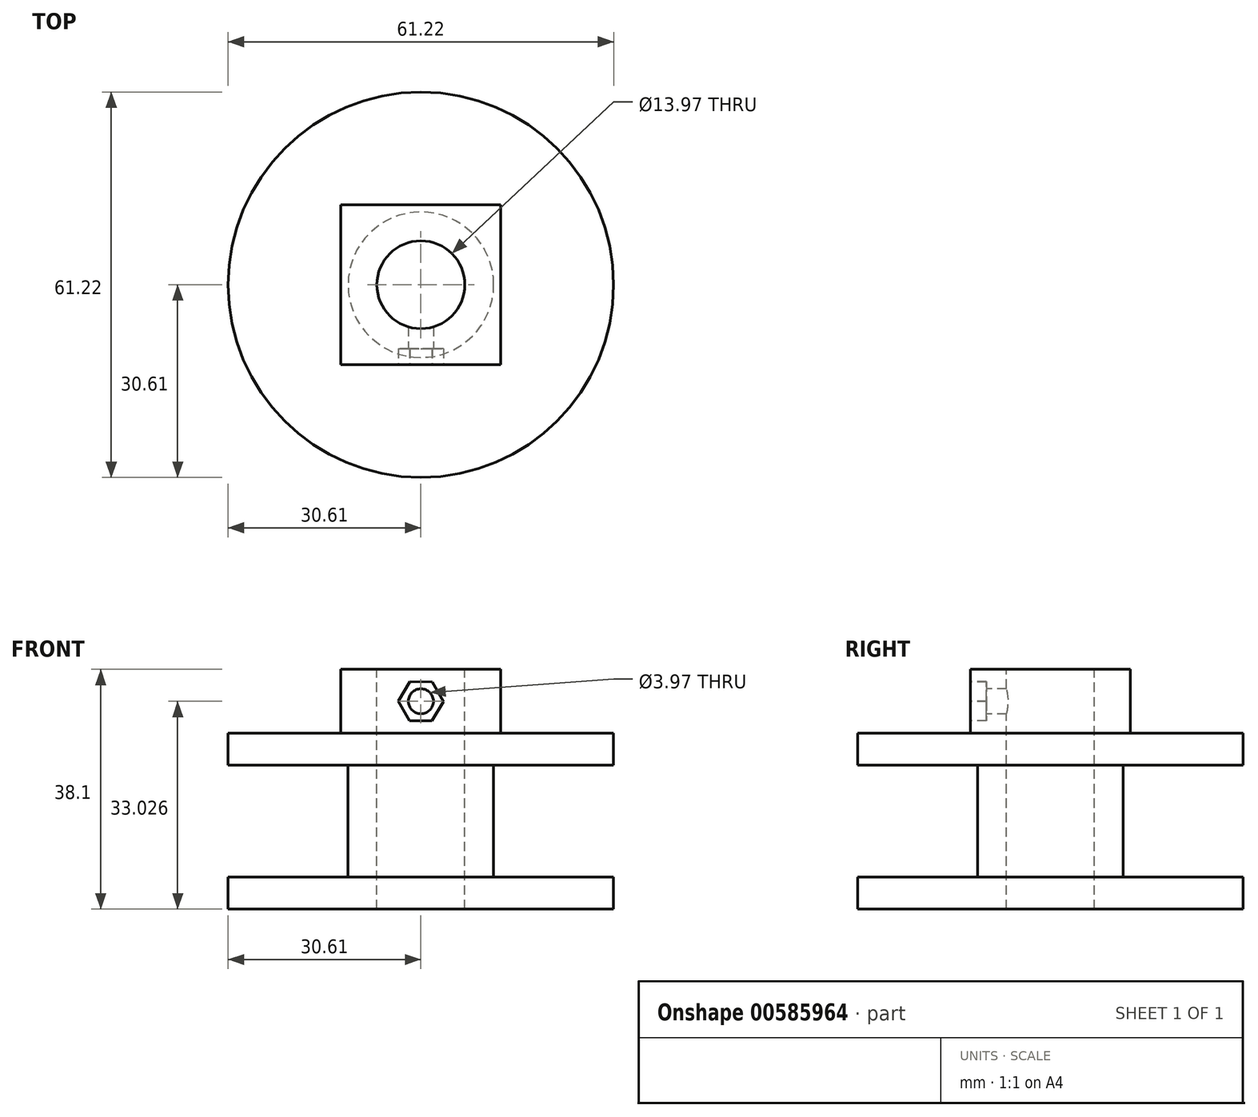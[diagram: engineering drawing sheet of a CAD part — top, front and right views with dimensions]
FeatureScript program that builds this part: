
annotation { "Feature Type Name" : "Feature", "Feature Type Description" : "" }
export const myFeature = defineFeature(function(context is Context, id is Id, definition is map)
    precondition{}
    {
        {
            var Q0;
            Q0=qCreatedBy(makeId("Front.planeOp"),FACE);
            var sketch = newSketch(context, id + "F0", { "sketchPlane" : qUnion([Q0])});
            skLineSegment(sketch, "E0.bottom", {"start": v(0, 0) * mm, "end": v(6.48, 0) * mm});
            skLineSegment(sketch, "E0.top", {"start": v(0, 38.1) * mm, "end": v(6.48, 38.1) * mm});
            skLineSegment(sketch, "E0.left", {"start": v(0, 0) * mm, "end": v(0, 38.1) * mm});
            skLineSegment(sketch, "E0.right", {"start": v(6.48, 0) * mm, "end": v(6.48, 38.1) * mm});
            skLineSegment(sketch, "E1.bottom", {"start": v(6.48, 38.1) * mm, "end": v(11.56, 38.1) * mm});
            skLineSegment(sketch, "E1.top", {"start": v(6.48, 0) * mm, "end": v(11.56, 0) * mm});
            skLineSegment(sketch, "E1.left", {"start": v(6.48, 38.1) * mm, "end": v(6.48, 0) * mm});
            skLineSegment(sketch, "E1.right", {"start": v(11.56, 38.1) * mm, "end": v(11.56, 0) * mm});
            skLineSegment(sketch, "E2.bottom", {"start": v(11.56, 0) * mm, "end": v(30.6, 0) * mm});
            skLineSegment(sketch, "E2.top", {"start": v(11.56, 5.08) * mm, "end": v(30.6, 5.08) * mm});
            skLineSegment(sketch, "E2.left", {"start": v(11.56, 0) * mm, "end": v(11.56, 5.08) * mm});
            skLineSegment(sketch, "E2.right", {"start": v(30.6, 0) * mm, "end": v(30.6, 5.08) * mm});
            skLineSegment(sketch, "E3", {"start": v(11.56, 5.08) * mm, "end": v(11.56, 22.86) * mm});
            skLineSegment(sketch, "E4.bottom", {"start": v(11.56, 22.86) * mm, "end": v(30.6, 22.86) * mm});
            skLineSegment(sketch, "E4.top", {"start": v(11.56, 27.94) * mm, "end": v(30.6, 27.94) * mm});
            skLineSegment(sketch, "E4.left", {"start": v(11.56, 22.86) * mm, "end": v(11.56, 27.94) * mm});
            skLineSegment(sketch, "E4.right", {"start": v(30.6, 22.86) * mm, "end": v(30.6, 27.94) * mm});
            skSolve(sketch);
        }
        {
            var Q0;
            Q0 = qSketchRegion(id + "F0", true);
            var Q1;
            Q1=sQuery(id+"F0.wireOp",EDGE,"E0.left");
            revolve(context, id + "F1", {"entities" : qUnion([Q0]), "axis" : qUnion([Q1]), "revolveType" : RevolveType.FULL});
        }
        {
            var Q0;
            Q0=makeQuery(id+"F1.opRevolve","SWEPT_FACE",FACE,{"disambiguationData":[OSD([sQuery(id+"F0.wireOp",EDGE,"E0.top"),sQuery(id+"F0.wireOp",EDGE,"E1.bottom")])]});
            var sketch = newSketch(context, id + "F2", { "sketchPlane" : qUnion([Q0])});
            skSolve(sketch);
        }
        {
            var Q0;
            Q0=makeQuery(id+"F2.imprint","IMPRINT",FACE,{"disambiguationData":[TD([[makeQuery(id+"F2.imprint","IMPRINT",EDGE,{"derivedFrom":makeQuery(id+"F1.opRevolve","SWEPT_EDGE",EDGE,{"disambiguationData":[OSD([sQuery(id+"F0.wireOp",EDGE,"E1.bottom"),sQuery(id+"F0.wireOp",EDGE,"E1.right")])]})}),-1.0]])]});
            var sketch = newSketch(context, id + "F3", { "sketchPlane" : qUnion([Q0])});
            skCircle(sketch, "E5", {"center": v(0, 0) * mm, "radius": 6.99 * mm});
            skSolve(sketch);
        }
        {
            var Q0;
            Q0=sQuery(id+"F3.wireOp",VERTEX,"E5.center");
            var Q1;
            Q1=makeQuery(id+"F1.opRevolve","SWEPT_BODY",BODY,{"disambiguationData":[OSD([sQuery(id+"F0.wireOp",EDGE,"E0.bottom"),sQuery(id+"F0.wireOp",EDGE,"E0.top"),sQuery(id+"F0.wireOp",EDGE,"E0.left"),sQuery(id+"F0.wireOp",EDGE,"E1.bottom"),sQuery(id+"F0.wireOp",EDGE,"E1.top"),sQuery(id+"F0.wireOp",EDGE,"E1.right"),sQuery(id+"F0.wireOp",EDGE,"E2.bottom"),sQuery(id+"F0.wireOp",EDGE,"E2.top"),sQuery(id+"F0.wireOp",EDGE,"E2.right"),sQuery(id+"F0.wireOp",EDGE,"E3"),sQuery(id+"F0.wireOp",EDGE,"E4.bottom"),sQuery(id+"F0.wireOp",EDGE,"E4.top"),sQuery(id+"F0.wireOp",EDGE,"E4.right")])]});
            hole(context, id + "F4", {"style" : HoleStyle.SIMPLE, "endStyle" : HoleEndStyle.THROUGH, "holeDiameter" : 13.97 * mm, "majorDiameter" : 6.35 * mm, "isTappedThrough" : true, "tappedDepth" : 12.7 * mm, "tapClearance" : 3, "locations" : qUnion([Q0]), "scope" : qUnion([Q1])});
        }
        {
            var Q0;
            Q0=makeQuery(id+"F1.opRevolve","SWEPT_FACE",FACE,{"disambiguationData":[OSD([sQuery(id+"F0.wireOp",EDGE,"E4.top")])]});
            var sketch = newSketch(context, id + "F5", { "sketchPlane" : qUnion([Q0])});
            skLineSegment(sketch, "E6.bottom", {"start": v(12.7, -12.7) * mm, "end": v(-12.7, -12.7) * mm});
            skLineSegment(sketch, "E6.top", {"start": v(12.7, 12.7) * mm, "end": v(-12.7, 12.7) * mm});
            skLineSegment(sketch, "E6.left", {"start": v(12.7, -12.7) * mm, "end": v(12.7, 12.7) * mm});
            skLineSegment(sketch, "E6.right", {"start": v(-12.7, -12.7) * mm, "end": v(-12.7, 12.7) * mm});
            skPoint(sketch, "E6.middle", {"position": v(0, 0) * mm});
            skSolve(sketch);
        }
        {
            var Q0;
            Q0=makeQuery(id+"F5.imprint","IMPRINT",FACE,{"disambiguationData":[TD([[makeQuery(id+"F5.imprint","IMPRINT",EDGE,{"derivedFrom":sQuery(id+"F5.wireOp",EDGE,"E6.bottom")}),-1.0]])]});
            extrude(context, id + "F6", {"entities" : qUnion([Q0]), "operationType" : NewBodyOperationType.ADD, "depth" : 10.16 * mm, "offsetDistance" : 25.4 * mm});
        }
        {
            var Q0;
            Q0=makeQuery(id+"F6.opExtrude","SWEPT_FACE",FACE,{"disambiguationData":[OSD([sQuery(id+"F5.wireOp",EDGE,"E6.bottom")])]});
            var sketch = newSketch(context, id + "F7", { "sketchPlane" : qUnion([Q0])});
            skCircle(sketch, "E7.cCircle", {"center": v(0, 33.02) * mm, "radius": 3.57 * mm, "construction": true});
            skLineSegment(sketch, "E7.0", {"start": v(1.76, 29.91) * mm, "end": v(-1.8, 29.94) * mm});
            skLineSegment(sketch, "E7.1", {"start": v(-1.8, 29.94) * mm, "end": v(-3.57, 33.05) * mm});
            skLineSegment(sketch, "E7.2", {"start": v(-3.57, 33.05) * mm, "end": v(-1.76, 36.13) * mm});
            skLineSegment(sketch, "E7.3", {"start": v(-1.76, 36.13) * mm, "end": v(1.8, 36.1) * mm});
            skLineSegment(sketch, "E7.4", {"start": v(1.8, 36.1) * mm, "end": v(3.57, 33) * mm});
            skLineSegment(sketch, "E7.5", {"start": v(3.57, 33) * mm, "end": v(1.76, 29.91) * mm});
            skSolve(sketch);
        }
        {
            var Q0;
            Q0=makeQuery(id+"F7.imprint","IMPRINT",FACE,{"disambiguationData":[TD([[makeQuery(id+"F7.imprint","IMPRINT",EDGE,{"derivedFrom":sQuery(id+"F7.wireOp",EDGE,"E7.0")}),-1.0]])]});
            extrude(context, id + "F8", {"entities" : qUnion([Q0]), "operationType" : NewBodyOperationType.REMOVE, "oppositeDirection" : true, "depth" : 2.54 * mm, "offsetDistance" : 25.4 * mm});
        }
        {
            var Q0;
            Q0=makeQuery(id+"F8.boolean.opBoolean","COPY",FACE,{"derivedFrom":makeQuery(id+"F8.opExtrude","CAP_FACE",FACE,{"disambiguationData":[OSD([sQuery(id+"F7.wireOp",EDGE,"E7.0"),sQuery(id+"F7.wireOp",EDGE,"E7.1"),sQuery(id+"F7.wireOp",EDGE,"E7.2"),sQuery(id+"F7.wireOp",EDGE,"E7.3"),sQuery(id+"F7.wireOp",EDGE,"E7.4"),sQuery(id+"F7.wireOp",EDGE,"E7.5")])],"isStart":false})});
            var sketch = newSketch(context, id + "F9", { "sketchPlane" : qUnion([Q0])});
            skCircle(sketch, "E8", {"center": v(0, 33.03) * mm, "radius": 1.98 * mm});
            skSolve(sketch);
        }
        {
            var Q0;
            Q0=makeQuery(id+"F9.imprint","IMPRINT",FACE,{"disambiguationData":[TD([[makeQuery(id+"F9.imprint","IMPRINT",EDGE,{"derivedFrom":sQuery(id+"F9.wireOp",EDGE,"E8")}),1.0]])]});
            extrude(context, id + "F10", {"entities" : qUnion([Q0]), "operationType" : NewBodyOperationType.REMOVE, "oppositeDirection" : true, "depth" : 5.08 * mm, "offsetDistance" : 25.4 * mm});
        }
    });
